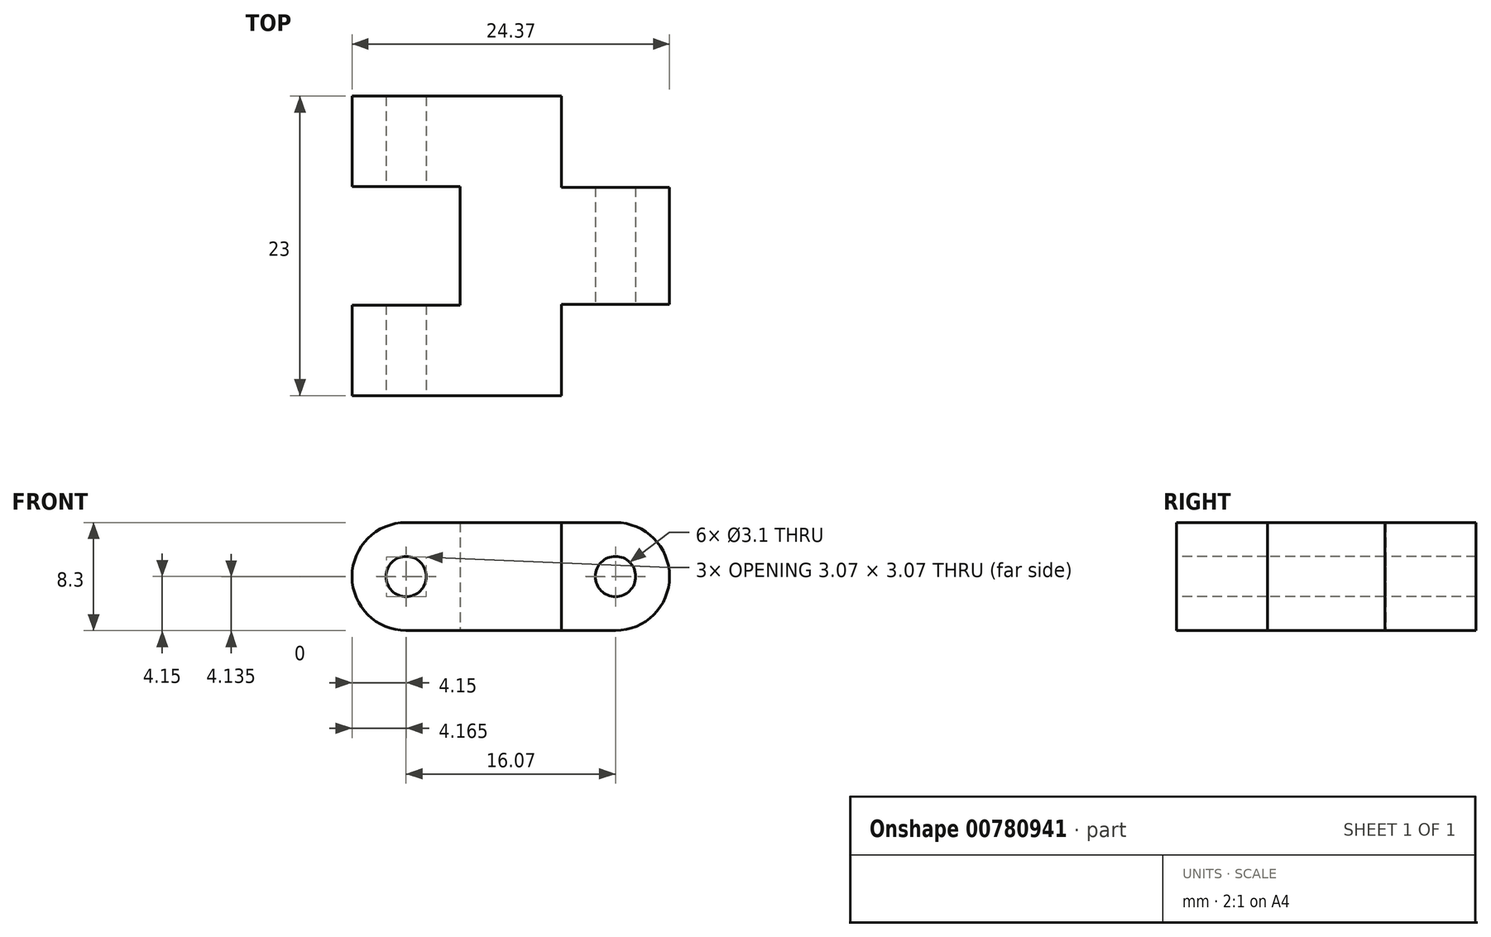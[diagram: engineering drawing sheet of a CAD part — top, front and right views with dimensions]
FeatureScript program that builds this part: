
annotation { "Feature Type Name" : "Feature", "Feature Type Description" : "" }
export const myFeature = defineFeature(function(context is Context, id is Id, definition is map)
    precondition{}
    {
        {
            var Q0;
            Q0=qCreatedBy(makeId("Top.planeOp"),FACE);
            var sketch = newSketch(context, id + "F0", { "sketchPlane" : qUnion([Q0])});
            skLineSegment(sketch, "E0", {"start": v(-65.82, -7.75) * mm, "end": v(-65.82, -14.7) * mm});
            skLineSegment(sketch, "E1", {"start": v(-65.82, -14.7) * mm, "end": v(-49.75, -14.7) * mm});
            skLineSegment(sketch, "E2", {"start": v(-49.75, -14.7) * mm, "end": v(-49.75, -7.7) * mm});
            skLineSegment(sketch, "E3", {"start": v(-49.75, -7.7) * mm, "end": v(-41.45, -7.7) * mm});
            skLineSegment(sketch, "E4", {"start": v(-41.45, -7.7) * mm, "end": v(-41.45, 1.3) * mm});
            skLineSegment(sketch, "E5", {"start": v(-41.45, 1.3) * mm, "end": v(-49.75, 1.3) * mm});
            skLineSegment(sketch, "E6", {"start": v(-49.75, 1.3) * mm, "end": v(-49.75, 8.3) * mm});
            skLineSegment(sketch, "E7", {"start": v(-49.75, 8.3) * mm, "end": v(-65.82, 8.3) * mm});
            skLineSegment(sketch, "E8", {"start": v(-65.82, 8.3) * mm, "end": v(-65.82, 1.35) * mm});
            skLineSegment(sketch, "E9", {"start": v(-65.82, 1.35) * mm, "end": v(-57.52, 1.35) * mm});
            skLineSegment(sketch, "E10", {"start": v(-57.52, 1.35) * mm, "end": v(-57.52, -7.75) * mm});
            skLineSegment(sketch, "E11", {"start": v(-57.52, -7.75) * mm, "end": v(-65.82, -7.75) * mm});
            skSolve(sketch);
        }
        {
            var Q0;
            Q0=makeQuery(id+"F0.imprint","IMPRINT",FACE,{"disambiguationData":[TD([[makeQuery(id+"F0.imprint","IMPRINT",EDGE,{"derivedFrom":sQuery(id+"F0.wireOp",EDGE,"E0")}),1.0]])]});
            extrude(context, id + "F1", {"entities" : qUnion([Q0]), "depth" : 8.3 * mm, "offsetDistance" : 25 * mm});
        }
        {
            var Q0;
            Q0=makeQuery(id+"F1.opExtrude","SWEPT_FACE",FACE,{"disambiguationData":[OSD([sQuery(id+"F0.wireOp",EDGE,"E1")])]});
            var sketch = newSketch(context, id + "F2", { "sketchPlane" : qUnion([Q0])});
            skCircle(sketch, "E12", {"center": v(-61.67, 4.15) * mm, "radius": 1.55 * mm});
            skPoint(sketch, "E12.centerSnap0", {"position": v(-65.82, 4.15) * mm});
            skSolve(sketch);
        }
        {
            var Q0;
            Q0=makeQuery(id+"F2.imprint","IMPRINT",FACE,{"disambiguationData":[TD([[makeQuery(id+"F2.imprint","IMPRINT",EDGE,{"derivedFrom":sQuery(id+"F2.wireOp",EDGE,"E12")}),1.0]])]});
            extrude(context, id + "F3", {"entities" : qUnion([Q0]), "operationType" : NewBodyOperationType.REMOVE, "endBound" : BoundingType.THROUGH_ALL, "oppositeDirection" : true, "depth" : 25 * mm, "offsetDistance" : 25 * mm});
        }
        {
            var Q0;
            Q0=makeQuery(id+"F1.opExtrude","SWEPT_FACE",FACE,{"disambiguationData":[OSD([sQuery(id+"F0.wireOp",EDGE,"E3")])]});
            var sketch = newSketch(context, id + "F4", { "sketchPlane" : qUnion([Q0])});
            skCircle(sketch, "E13", {"center": v(-45.6, 4.15) * mm, "radius": 1.55 * mm});
            skPoint(sketch, "E13.centerSnap0", {"position": v(-41.45, 4.15) * mm});
            skSolve(sketch);
        }
        {
            var Q0;
            Q0=makeQuery(id+"F4.imprint","IMPRINT",FACE,{"disambiguationData":[TD([[makeQuery(id+"F4.imprint","IMPRINT",EDGE,{"derivedFrom":sQuery(id+"F4.wireOp",EDGE,"E13")}),1.0]])]});
            extrude(context, id + "F5", {"entities" : qUnion([Q0]), "operationType" : NewBodyOperationType.REMOVE, "endBound" : BoundingType.THROUGH_ALL, "oppositeDirection" : true, "depth" : 25 * mm, "offsetDistance" : 25 * mm});
        }
        {
            var Q0;
            Q0=makeQuery(id+"F1.opExtrude","CAP_EDGE",EDGE,{"disambiguationData":[OSD([sQuery(id+"F0.wireOp",EDGE,"E8")])],"isStart":false});
            var Q1;
            Q1=makeQuery(id+"F1.opExtrude","CAP_EDGE",EDGE,{"disambiguationData":[OSD([sQuery(id+"F0.wireOp",EDGE,"E8")])],"isStart":true});
            var Q2;
            Q2=makeQuery(id+"F1.opExtrude","CAP_EDGE",EDGE,{"disambiguationData":[OSD([sQuery(id+"F0.wireOp",EDGE,"E0")])],"isStart":true});
            var Q3;
            Q3=makeQuery(id+"F1.opExtrude","CAP_EDGE",EDGE,{"disambiguationData":[OSD([sQuery(id+"F0.wireOp",EDGE,"E0")])],"isStart":false});
            var Q4;
            Q4=makeQuery(id+"F1.opExtrude","CAP_EDGE",EDGE,{"disambiguationData":[OSD([sQuery(id+"F0.wireOp",EDGE,"E4")])],"isStart":true});
            var Q5;
            Q5=makeQuery(id+"F1.opExtrude","CAP_EDGE",EDGE,{"disambiguationData":[OSD([sQuery(id+"F0.wireOp",EDGE,"E4")])],"isStart":false});
            fillet(context, id + "F6", {"entities" : qUnion([Q0, Q1, Q2, Q3, Q4, Q5]), "radius" : 4.15 * mm, "tangentPropagation" : true, "allowEdgeOverflow" : false});
        }
    });
